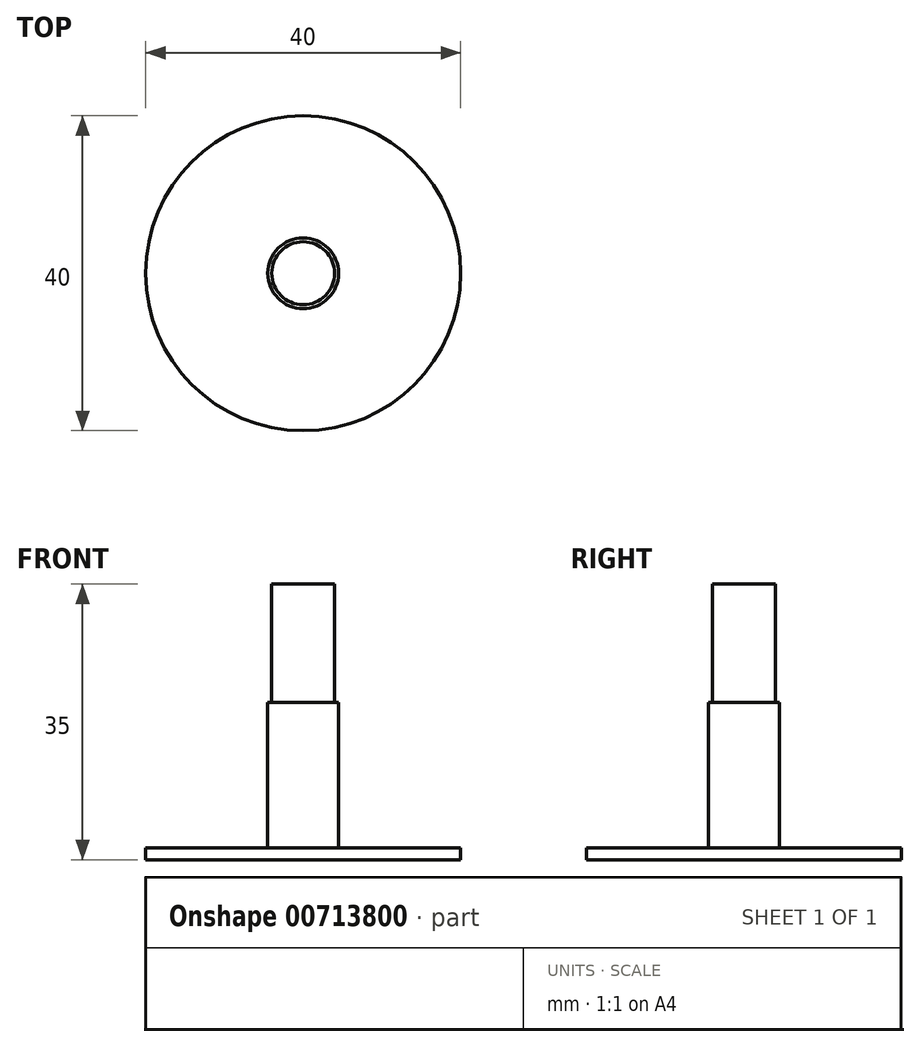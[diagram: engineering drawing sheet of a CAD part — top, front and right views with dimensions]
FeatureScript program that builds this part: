
annotation { "Feature Type Name" : "Feature", "Feature Type Description" : "" }
export const myFeature = defineFeature(function(context is Context, id is Id, definition is map)
    precondition{}
    {
        {
            var Q0;
            Q0=qCreatedBy(makeId("Front.planeOp"),FACE);
            var sketch = newSketch(context, id + "F0", { "sketchPlane" : qUnion([Q0])});
            skLineSegment(sketch, "E0", {"start": v(0, 0) * mm, "end": v(4.5, 0) * mm});
            skLineSegment(sketch, "E1", {"start": v(4.5, 0) * mm, "end": v(4.5, 20) * mm});
            skLineSegment(sketch, "E2", {"start": v(4.5, 20) * mm, "end": v(4, 20) * mm});
            skLineSegment(sketch, "E3", {"start": v(4, 20) * mm, "end": v(4, 27) * mm});
            skLineSegment(sketch, "E4", {"start": v(4, 27) * mm, "end": v(4, 35) * mm});
            skLineSegment(sketch, "E5", {"start": v(0, 0) * mm, "end": v(20, 0) * mm});
            skLineSegment(sketch, "E6", {"start": v(20, 0) * mm, "end": v(20, 1.5) * mm});
            skLineSegment(sketch, "E7", {"start": v(20, 1.5) * mm, "end": v(4.5, 1.5) * mm});
            skLineSegment(sketch, "E8", {"start": v(4, 35) * mm, "end": v(0, 35) * mm});
            skLineSegment(sketch, "E9", {"start": v(0, 35) * mm, "end": v(0, 0) * mm});
            skSolve(sketch);
        }
        {
            var Q0;
            Q0 = qSketchRegion(id + "F0", true);
            var Q1;
            Q1=sQuery(id+"F0.wireOp",EDGE,"E9");
            revolve(context, id + "F1", {"surfaceOperationType" : NewSurfaceOperationType.NEW, "entities" : qUnion([Q0]), "axis" : qUnion([Q1]), "revolveType" : RevolveType.FULL});
        }
    });
